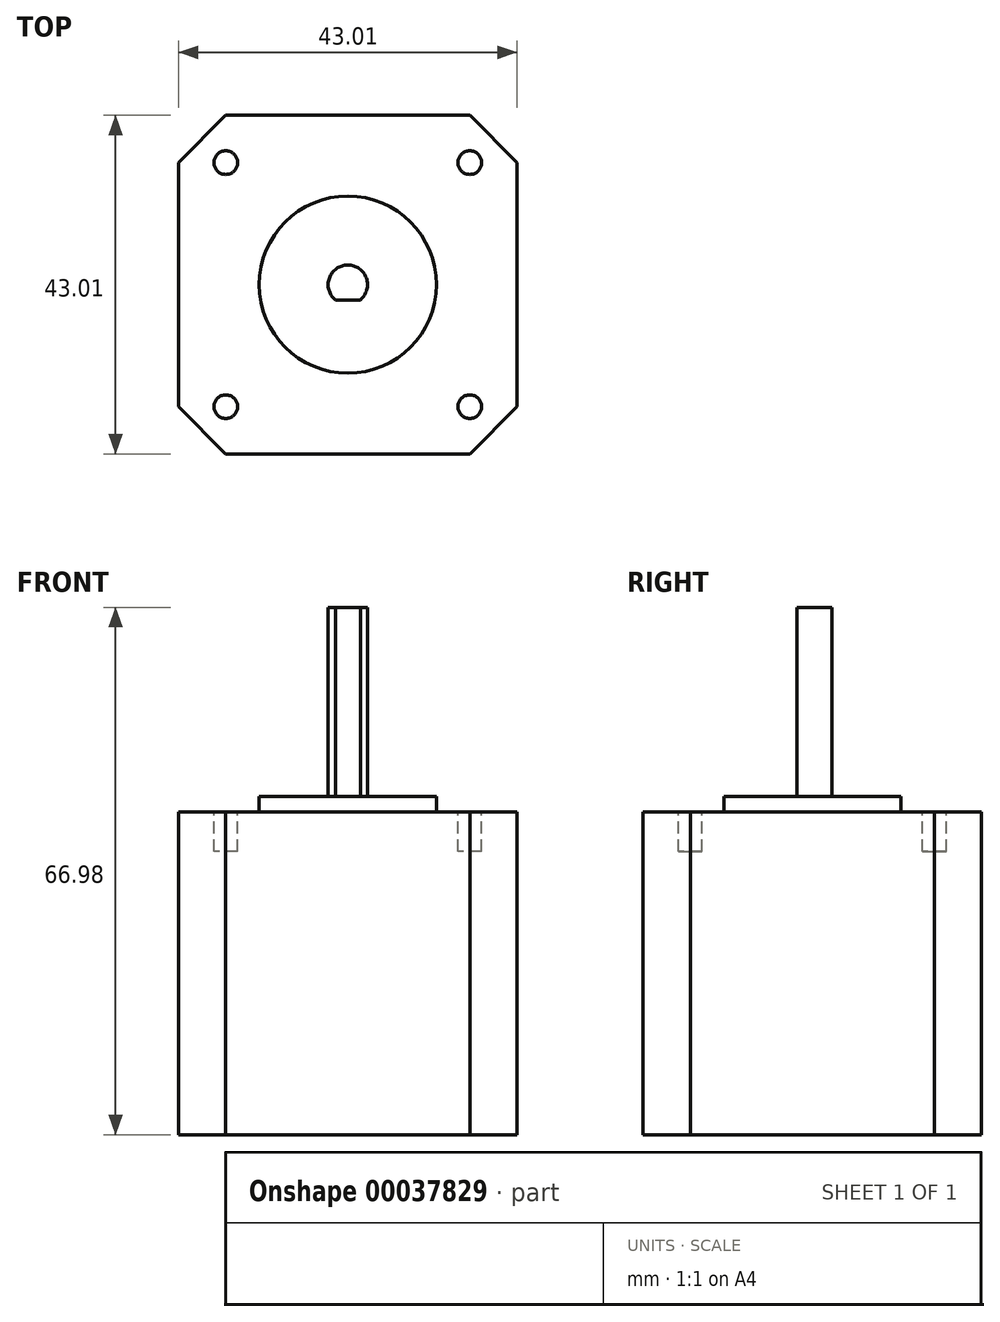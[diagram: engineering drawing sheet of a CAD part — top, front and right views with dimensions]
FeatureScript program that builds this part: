
annotation { "Feature Type Name" : "Feature", "Feature Type Description" : "" }
export const myFeature = defineFeature(function(context is Context, id is Id, definition is map)
    precondition{}
    {
        {
            var Q0;
            Q0=qCreatedBy(makeId("Top.planeOp"),FACE);
            var sketch = newSketch(context, id + "F0", { "sketchPlane" : qUnion([Q0])});
            skLineSegment(sketch, "E0.bottom", {"start": v(0, 0) * mm, "end": v(43, 0) * mm});
            skLineSegment(sketch, "E0.top", {"start": v(0, 43) * mm, "end": v(43, 43) * mm});
            skLineSegment(sketch, "E0.left", {"start": v(0, 0) * mm, "end": v(0, 43) * mm});
            skLineSegment(sketch, "E0.right", {"start": v(43, 0) * mm, "end": v(43, 43) * mm});
            skSolve(sketch);
        }
        {
            var Q0;
            Q0=makeQuery(id+"F0.imprint","IMPRINT",FACE,{"disambiguationData":[TD([[makeQuery(id+"F0.imprint","IMPRINT",EDGE,{"derivedFrom":sQuery(id+"F0.wireOp",EDGE,"E0.bottom")}),1.0]])]});
            extrude(context, id + "F1", {"entities" : qUnion([Q0]), "depth" : 40.98 * mm});
        }
        {
            var Q0;
            Q0=makeQuery(id+"F1.opExtrude","CAP_FACE",FACE,{"disambiguationData":[OSD([sQuery(id+"F0.wireOp",EDGE,"E0.bottom"),sQuery(id+"F0.wireOp",EDGE,"E0.top"),sQuery(id+"F0.wireOp",EDGE,"E0.left"),sQuery(id+"F0.wireOp",EDGE,"E0.right")])],"isStart":false});
            var sketch = newSketch(context, id + "F2", { "sketchPlane" : qUnion([Q0])});
            skLineSegment(sketch, "E1", {"start": v(21.5, 0) * mm, "end": v(21.5, 43) * mm});
            skCircle(sketch, "E2", {"center": v(21.5, 21.5) * mm, "radius": 11.25 * mm});
            skSolve(sketch);
        }
        {
            var Q0;
            {var subQ0=sQuery(id+"F2.wireOp",EDGE,"E2");var subQ1=sQuery(id+"F2.wireOp",EDGE,"E1");var subQ3=makeQuery(id+"F2.imprint","INTERSECT",VERTEX,{"disambiguationData":[OD(0.0)],"derivedFrom":[subQ1,subQ0]});var subQ4=makeQuery(id+"F2.imprint","IMPRINT",EDGE,{"disambiguationData":[TD([[subQ3,-1.0]])],"derivedFrom":subQ1});Q0=qUnion([makeQuery(id+"F2.imprint","IMPRINT",FACE,{"disambiguationData":[TD([[subQ4,1.0]])]}),makeQuery(id+"F2.imprint","IMPRINT",FACE,{"disambiguationData":[TD([[subQ4,-1.0]])]})]);}
            extrude(context, id + "F3", {"entities" : qUnion([Q0]), "operationType" : NewBodyOperationType.ADD, "depth" : 2 * mm});
        }
        {
            var Q0;
            Q0=makeQuery(id+"F1.opExtrude","CAP_FACE",FACE,{"disambiguationData":[OSD([sQuery(id+"F0.wireOp",EDGE,"E0.bottom"),sQuery(id+"F0.wireOp",EDGE,"E0.top"),sQuery(id+"F0.wireOp",EDGE,"E0.left"),sQuery(id+"F0.wireOp",EDGE,"E0.right")])],"isStart":false});
            var sketch = newSketch(context, id + "F4", { "sketchPlane" : qUnion([Q0])});
            skLineSegment(sketch, "E3", {"start": v(6, 21.5) * mm, "end": v(37, 21.5) * mm});
            skLineSegment(sketch, "E4", {"start": v(37, 37) * mm, "end": v(37, 6) * mm});
            skLineSegment(sketch, "E5", {"start": v(6, 37) * mm, "end": v(6, 6) * mm});
            skPoint(sketch, "E6", {"position": v(21.5, 21.5) * mm});
            skCircle(sketch, "E7", {"center": v(6, 6) * mm, "radius": 1.5 * mm});
            skCircle(sketch, "E8", {"center": v(37, 6) * mm, "radius": 1.5 * mm});
            skCircle(sketch, "E9", {"center": v(37, 37) * mm, "radius": 1.5 * mm});
            skCircle(sketch, "E10", {"center": v(6, 37) * mm, "radius": 1.5 * mm});
            skLineSegment(sketch, "E11", {"start": v(21.5, 21.5) * mm, "end": v(21.5, 0) * mm});
            skSolve(sketch);
        }
        {
            var Q0;
            {var subQ0=sQuery(id+"F4.wireOp",EDGE,"E9");var subQ2=sQuery(id+"F4.wireOp",EDGE,"E8");var subQ3=sQuery(id+"F4.wireOp",EDGE,"E10");var subQ5=sQuery(id+"F4.wireOp",EDGE,"E7");Q0=qUnion([makeQuery(id+"F4.imprint","IMPRINT",FACE,{"disambiguationData":[TD([[makeQuery(id+"F4.imprint","IMPRINT",EDGE,{"derivedFrom":subQ0}),1.0]])]}),makeQuery(id+"F4.imprint","IMPRINT",FACE,{"disambiguationData":[TD([[makeQuery(id+"F4.imprint","IMPRINT",EDGE,{"derivedFrom":subQ2}),1.0]])]}),makeQuery(id+"F4.imprint","IMPRINT",FACE,{"disambiguationData":[TD([[makeQuery(id+"F4.imprint","IMPRINT",EDGE,{"derivedFrom":subQ3}),1.0]])]}),makeQuery(id+"F4.imprint","IMPRINT",FACE,{"disambiguationData":[TD([[makeQuery(id+"F4.imprint","IMPRINT",EDGE,{"derivedFrom":subQ5}),1.0]])]})]);}
            extrude(context, id + "F5", {"entities" : qUnion([Q0]), "operationType" : NewBodyOperationType.REMOVE, "oppositeDirection" : true, "depth" : 5 * mm});
        }
        {
            var Q0;
            Q0=makeQuery(id+"F3.opExtrude","CAP_FACE",FACE,{"disambiguationData":[OSD([sQuery(id+"F2.wireOp",EDGE,"E2")])],"isStart":false});
            var sketch = newSketch(context, id + "F6", { "sketchPlane" : qUnion([Q0])});
            skArc(sketch, "E12", {"start": v(23.1, 19.57) * mm, "mid": v(21.5, 24) * mm, "end": v(19.92, 19.57) * mm});
            skLineSegment(sketch, "E13", {"start": v(19.92, 19.57) * mm, "end": v(23.1, 19.57) * mm});
            skLineSegment(sketch, "E14", {"start": v(21.5, 19.57) * mm, "end": v(21.5, 21.5) * mm, "construction": true});
            skSolve(sketch);
        }
        {
            var Q0;
            Q0=qSketchRegion(id+"F6",true);
            extrude(context, id + "F7", {"entities" : qUnion([Q0]), "operationType" : NewBodyOperationType.ADD, "depth" : 24 * mm});
        }
        {
            var Q0;
            Q0=makeQuery(id+"F1.opExtrude","SWEPT_EDGE",EDGE,{"disambiguationData":[OSD([sQuery(id+"F0.wireOp",EDGE,"E0.top"),sQuery(id+"F0.wireOp",EDGE,"E0.left")])]});
            var Q1;
            Q1=makeQuery(id+"F1.opExtrude","SWEPT_EDGE",EDGE,{"disambiguationData":[OSD([sQuery(id+"F0.wireOp",EDGE,"E0.bottom"),sQuery(id+"F0.wireOp",EDGE,"E0.left")])]});
            var Q2;
            Q2=makeQuery(id+"F1.opExtrude","SWEPT_EDGE",EDGE,{"disambiguationData":[OSD([sQuery(id+"F0.wireOp",EDGE,"E0.bottom"),sQuery(id+"F0.wireOp",EDGE,"E0.right")])]});
            var Q3;
            Q3=makeQuery(id+"F1.opExtrude","SWEPT_EDGE",EDGE,{"disambiguationData":[OSD([sQuery(id+"F0.wireOp",EDGE,"E0.top"),sQuery(id+"F0.wireOp",EDGE,"E0.right")])]});
            chamfer(context, id + "F8", {"entities" : qUnion([Q0, Q1, Q2, Q3]), "width" : 6 * mm, "tangentPropagation" : true});
        }
    });
